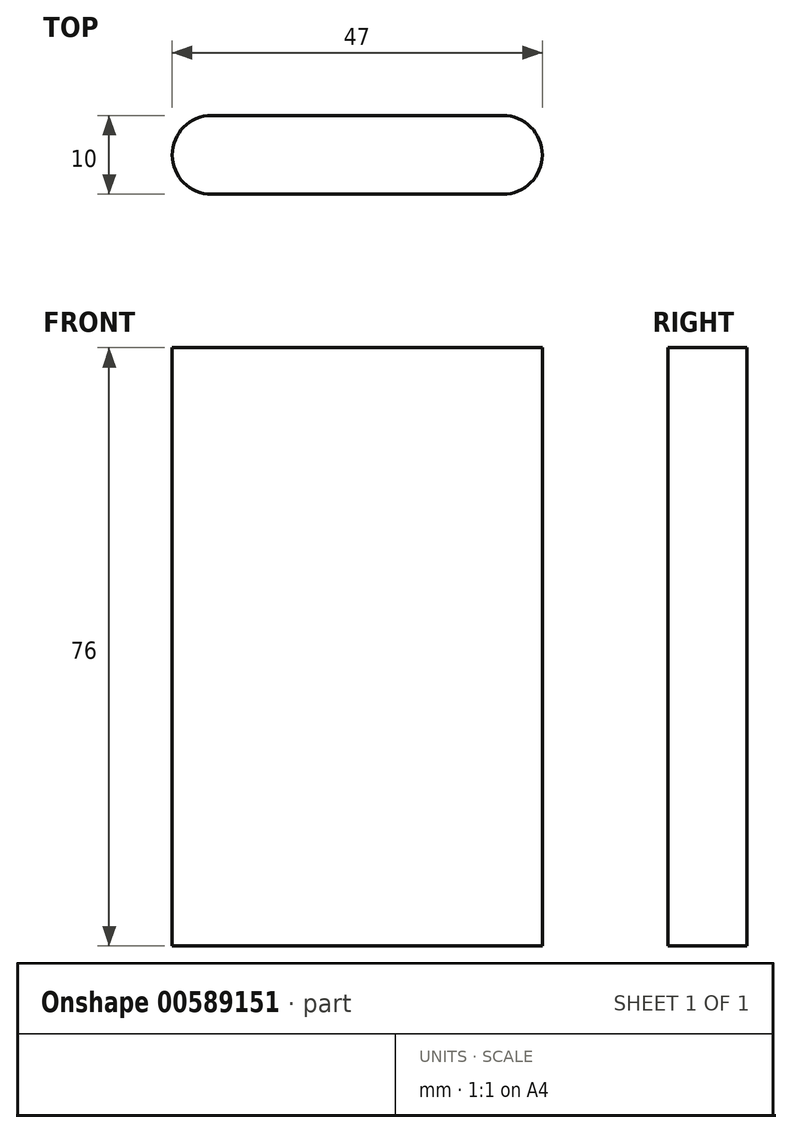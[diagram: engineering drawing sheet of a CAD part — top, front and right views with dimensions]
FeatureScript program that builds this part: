
annotation { "Feature Type Name" : "Feature", "Feature Type Description" : "" }
export const myFeature = defineFeature(function(context is Context, id is Id, definition is map)
    precondition{}
    {
        {
            var Q0;
            Q0=qCreatedBy(makeId("Top.planeOp"),FACE);
            var sketch = newSketch(context, id + "F0", { "sketchPlane" : qUnion([Q0])});
            skLineSegment(sketch, "E0.bottom", {"start": v(18.5, -5) * mm, "end": v(-18.5, -5) * mm});
            skLineSegment(sketch, "E0.top", {"start": v(18.5, 5) * mm, "end": v(-18.5, 5) * mm});
            skLineSegment(sketch, "E0.left", {"start": v(23.5, 0) * mm, "end": v(23.5, 0) * mm});
            skLineSegment(sketch, "E0.right", {"start": v(-23.5, 0) * mm, "end": v(-23.5, 0) * mm});
            skPoint(sketch, "E0.middle", {"position": v(0, 0) * mm});
            skPoint(sketch, "E1.visualSharp", {"position": v(-23.5, 5) * mm});
            skArc(sketch, "E1.filletArc", {"start": v(-18.5, 5) * mm, "mid": v(-22.04, 3.54) * mm, "end": v(-23.5, 0) * mm});
            skPoint(sketch, "E2.visualSharp", {"position": v(-23.5, -5) * mm});
            skArc(sketch, "E2.filletArc", {"start": v(-23.5, 0) * mm, "mid": v(-22.04, -3.54) * mm, "end": v(-18.5, -5) * mm});
            skPoint(sketch, "E3.visualSharp", {"position": v(23.5, 5) * mm});
            skArc(sketch, "E3.filletArc", {"start": v(23.5, 0) * mm, "mid": v(22.04, 3.54) * mm, "end": v(18.5, 5) * mm});
            skPoint(sketch, "E4.visualSharp", {"position": v(23.5, -5) * mm});
            skArc(sketch, "E4.filletArc", {"start": v(18.5, -5) * mm, "mid": v(22.04, -3.54) * mm, "end": v(23.5, 0) * mm});
            skSolve(sketch);
        }
        {
            var Q0;
            Q0 = qSketchRegion(id + "F0", true);
            extrude(context, id + "F1", {"entities" : qUnion([Q0]), "depth" : 76 * mm, "offsetDistance" : 25.4 * mm});
        }
    });
